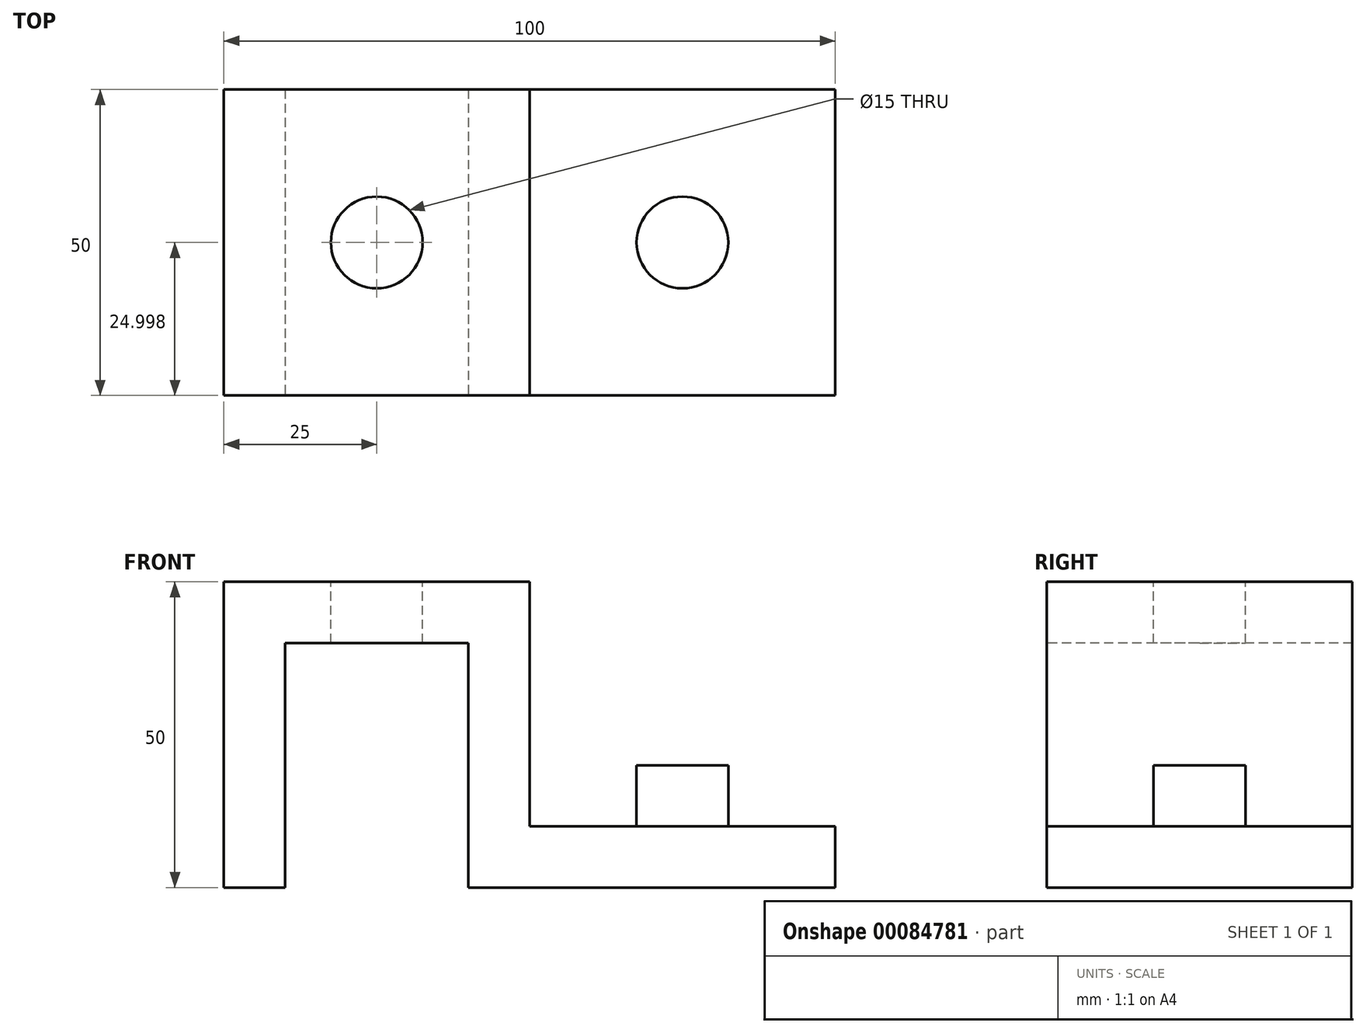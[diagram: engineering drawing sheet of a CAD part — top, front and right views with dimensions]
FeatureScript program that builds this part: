
annotation { "Feature Type Name" : "Feature", "Feature Type Description" : "" }
export const myFeature = defineFeature(function(context is Context, id is Id, definition is map)
    precondition{}
    {
        {
            var Q0;
            Q0=qCreatedBy(makeId("Front.planeOp"),FACE);
            var sketch = newSketch(context, id + "F0", { "sketchPlane" : qUnion([Q0])});
            skLineSegment(sketch, "E0", {"start": v(0, 0) * mm, "end": v(0, 50) * mm});
            skLineSegment(sketch, "E1", {"start": v(0, 50) * mm, "end": v(50, 50) * mm});
            skLineSegment(sketch, "E2", {"start": v(50, 50) * mm, "end": v(50, 10) * mm});
            skLineSegment(sketch, "E3", {"start": v(50, 10) * mm, "end": v(100, 10) * mm});
            skLineSegment(sketch, "E4", {"start": v(100, 10) * mm, "end": v(100, 0) * mm});
            skLineSegment(sketch, "E5", {"start": v(100, 0) * mm, "end": v(0, 0) * mm});
            skSolve(sketch);
        }
        {
            var Q0;
            Q0=makeQuery(id+"F0.imprint","IMPRINT",FACE,{"disambiguationData":[TD([[makeQuery(id+"F0.imprint","IMPRINT",EDGE,{"derivedFrom":sQuery(id+"F0.wireOp",EDGE,"E0")}),-1.0]])]});
            extrude(context, id + "F1", {"entities" : qUnion([Q0]), "depth" : 50 * mm});
        }
        {
            var Q0;
            Q0=makeQuery(id+"F1.opExtrude","CAP_FACE",FACE,{"disambiguationData":[OSD([sQuery(id+"F0.wireOp",EDGE,"E0"),sQuery(id+"F0.wireOp",EDGE,"E1"),sQuery(id+"F0.wireOp",EDGE,"E2"),sQuery(id+"F0.wireOp",EDGE,"E3"),sQuery(id+"F0.wireOp",EDGE,"E4"),sQuery(id+"F0.wireOp",EDGE,"E5")])],"isStart":false});
            var sketch = newSketch(context, id + "F2", { "sketchPlane" : qUnion([Q0])});
            skLineSegment(sketch, "E6.bottom", {"start": v(10, 40) * mm, "end": v(40, 40) * mm});
            skLineSegment(sketch, "E6.top", {"start": v(10, 0) * mm, "end": v(40, 0) * mm});
            skLineSegment(sketch, "E6.left", {"start": v(10, 40) * mm, "end": v(10, 0) * mm});
            skLineSegment(sketch, "E6.right", {"start": v(40, 40) * mm, "end": v(40, 0) * mm});
            skSolve(sketch);
        }
        {
            var Q0;
            Q0 = qSketchRegion(id + "F2", true);
            extrude(context, id + "F3", {"entities" : qUnion([Q0]), "operationType" : NewBodyOperationType.REMOVE, "endBound" : BoundingType.THROUGH_ALL, "oppositeDirection" : true, "depth" : 25 * mm});
        }
        {
            var Q0;
            Q0=makeQuery(id+"F1.opExtrude","SWEPT_FACE",FACE,{"disambiguationData":[OSD([sQuery(id+"F0.wireOp",EDGE,"E1")])]});
            var sketch = newSketch(context, id + "F4", { "sketchPlane" : qUnion([Q0])});
            skPoint(sketch, "E7.endSnap0", {"position": v(50, -25) * mm});
            skPoint(sketch, "E8.center.orphan", {"position": v(25, -25) * mm});
            skPoint(sketch, "E9.trimOffspring.end.orphan", {"position": v(99.77, -25) * mm});
            skPoint(sketch, "E7.start.orphan", {"position": v(0, -25) * mm});
            skLineSegment(sketch, "E10", {"start": v(0, -25) * mm, "end": v(99.77, -25) * mm, "construction": true});
            skCircle(sketch, "E11", {"center": v(25, -25) * mm, "radius": 7.5 * mm});
            skSolve(sketch);
        }
        {
            var Q0;
            Q0 = qSketchRegion(id + "F4", true);
            extrude(context, id + "F5", {"entities" : qUnion([Q0]), "operationType" : NewBodyOperationType.REMOVE, "endBound" : BoundingType.THROUGH_ALL, "oppositeDirection" : true, "depth" : 25 * mm});
        }
        {
            var Q0;
            {var subQ0=sQuery(id+"F0.wireOp",EDGE,"E5");var subQ1=sQuery(id+"F0.wireOp",EDGE,"E4");Q0=makeQuery(id+"F3.boolean.opBoolean","SPLIT",FACE,{"disambiguationData":[TD([makeQuery(id+"F1.opExtrude","SWEPT_FACE",FACE,{"disambiguationData":[OSD([subQ1])]})])],"derivedFrom":makeQuery(id+"F1.opExtrude","SWEPT_FACE",FACE,{"disambiguationData":[OSD([subQ0])]})});}
            var sketch = newSketch(context, id + "F6", { "sketchPlane" : qUnion([Q0])});
            skLineSegment(sketch, "E12", {"start": v(100, 25) * mm, "end": v(0, 25) * mm, "construction": true});
            skCircle(sketch, "E13", {"center": v(75, 25) * mm, "radius": 7.5 * mm});
            skSolve(sketch);
        }
        {
            var Q0;
            Q0 = qSketchRegion(id + "F6", true);
            extrude(context, id + "F7", {"entities" : qUnion([Q0]), "operationType" : NewBodyOperationType.ADD, "oppositeDirection" : true, "depth" : 20 * mm});
        }
    });
